# Revit family: Interrata - Copy - Copy (2)
name_source: partatom
category: Lighting Fixtures
revit_build: Autodesk Revit 2017 (Build: 20190507_1515(x64)
units: mm (PartAtom-declared; Revit-internal decimal feet)

## family parameters
Cut with Voids When Loaded = No
Host = Face
Light Source = No
OmniClass Number = 23.80.70.00
OmniClass Title = Lighting
Part Type = Normal
Room Calculation Point = No
Round Connector Dimension = Use Diameter
Shared = No

## types (10) — shared parameters
Apparent Load = 0 VA
Assembly Code = D5020200
BodyThickness_SYL = 3 mm  [stored 0.00984252 ft]
Chamfer_SYL = 2 mm  [stored 0.00656168 ft]
ClassificationName = Uniclass2015
ClassificationValue = EF_70_80
Default Elevation = 100 mm
IfcExportAs = IfcLightFixtureType
IfcExportType = IfcLightFixtureType
Keynote = 16500
Manufacturer = Feilo Sylvania
ManufacturerName = Feilo Sylvania
Material_1_SYL = Stainless Steel
Material_2_SYL = Polycarbonate, Clear
Material_3_SYL = <By Category>
Material_4_SYL = <By Category>
Thickness_SYL = 3 mm  [stored 0.00984252 ft]
Type Image = <None>
URL = http://www.sylvania-lighting.com
Voltage = 0 V
zero-valued in all types: Cost, NominalDepth, NominalHeight, NominalLength, PowerFactor

## per-type parameters (varying)
| type | BodyHeight1_SYL | BodyHeight2_SYL | BodyHeight3_SYL | BodyHeight4_SYL | BodyRad1_SYL | BodyRad2_SYL | BodyRad_SYL | DiffuserRad_SYL | L_SYL | Radius2_SYL | Radius3_SYL | Radius_SYL | RevolutionAxisFromRefLevel_SYL | RingHeight_SYL | S_SYL | Step1_SYL | Step2_SYL | TypeLamp_SYL | XS_SYL |
| 0049036 | 5 mm  [stored 0.0164042 ft] | 5 mm  [stored 0.0164042 ft] | 80 mm  [stored 0.262467 ft] | 6 mm  [stored 0.019685 ft] | 24 mm  [stored 0.0787402 ft] | 17 mm | 30 mm  [stored 0.0984252 ft] | 21 mm  [stored 0.0688976 ft] | No | 34 mm | 32 mm  [stored 0.104987 ft] | 50 mm  [stored 0.164042 ft] | 27 mm  [stored 0.0885827 ft] | 3 mm  [stored 0.00984252 ft] | No | 26 mm | 100 mm | Interrata Lamp : 0049036 INTERRATA XS  FROSTED 100LM 830 | Yes |
| 0049042 | 10 mm  [stored 0.0328084 ft] | 20 mm  [stored 0.0656168 ft] | 29 mm  [stored 0.0951444 ft] | 67 mm | 69 mm | 55 mm  [stored 0.180446 ft] | 95 mm | 66 mm  [stored 0.216535 ft] | No | 98 mm  [stored 0.321522 ft] | 96 mm  [stored 0.314961 ft] | 100 mm | 60 mm  [stored 0.19685 ft] | 3 mm  [stored 0.00984252 ft] | No | 18 mm | 206 mm | Interrata Lamp : 0049042 INTERRATA ADJUSTABLE M  CL 1000LM 830 MB | No |
| 0049043 | 10 mm  [stored 0.0328084 ft] | 20 mm  [stored 0.0656168 ft] | 29 mm  [stored 0.0951444 ft] | 67 mm | 69 mm | 55 mm  [stored 0.180446 ft] | 95 mm | 66 mm  [stored 0.216535 ft] | No | 98 mm  [stored 0.321522 ft] | 96 mm  [stored 0.314961 ft] | 100 mm | 60 mm  [stored 0.19685 ft] | 3 mm  [stored 0.00984252 ft] | No | 18 mm | 206 mm | Interrata Lamp : 0049043 INTERRATA ADJUSTABLE M  CL 1000LM 840 MB | No |
| 0049044 | 14 mm  [stored 0.0459318 ft] | 34 mm | 21 mm  [stored 0.0688976 ft] | 82 mm  [stored 0.269029 ft] | 99 mm | 83 mm | 120 mm | 94 mm  [stored 0.308399 ft] | Yes | 124 mm | 112 mm | 130 mm | 74 mm  [stored 0.242782 ft] | 4 mm  [stored 0.0131234 ft] | No | 20 mm  [stored 0.0656168 ft] | 236 mm | Interrata Lamp : 0049044 INTERRATA ADJUSTABLE L  CL 2000LM 830 MB | No |
| 0049037 | 5 mm  [stored 0.0164042 ft] | 5 mm  [stored 0.0164042 ft] | 80 mm  [stored 0.262467 ft] | 6 mm  [stored 0.019685 ft] | 24 mm  [stored 0.0787402 ft] | 17 mm | 30 mm  [stored 0.0984252 ft] | 21 mm  [stored 0.0688976 ft] | No | 34 mm | 32 mm  [stored 0.104987 ft] | 50 mm  [stored 0.164042 ft] | 27 mm  [stored 0.0885827 ft] | 3 mm  [stored 0.00984252 ft] | No | 26 mm | 100 mm | Interrata Lamp : 0049037 INTERRATA XS  FROSTED 100LM 840 | Yes |
| 0049039 | 5 mm  [stored 0.0164042 ft] | 5 mm  [stored 0.0164042 ft] | 80 mm  [stored 0.262467 ft] | 6 mm  [stored 0.019685 ft] | 24 mm  [stored 0.0787402 ft] | 17 mm | 30 mm  [stored 0.0984252 ft] | 21 mm  [stored 0.0688976 ft] | No | 34 mm | 32 mm  [stored 0.104987 ft] | 50 mm  [stored 0.164042 ft] | 27 mm  [stored 0.0885827 ft] | 3 mm  [stored 0.00984252 ft] | No | 26 mm | 100 mm | Interrata Lamp : 0049039 INTERRATA XS  CLEAR 100LM 840 NB | Yes |
| 0049038 | 5 mm  [stored 0.0164042 ft] | 5 mm  [stored 0.0164042 ft] | 80 mm  [stored 0.262467 ft] | 6 mm  [stored 0.019685 ft] | 24 mm  [stored 0.0787402 ft] | 17 mm | 30 mm  [stored 0.0984252 ft] | 21 mm  [stored 0.0688976 ft] | No | 34 mm | 32 mm  [stored 0.104987 ft] | 50 mm  [stored 0.164042 ft] | 27 mm  [stored 0.0885827 ft] | 3 mm  [stored 0.00984252 ft] | No | 26 mm | 100 mm | Interrata Lamp : 0049038 INTERRATA XS  CLEAR 100LM 830 NB | Yes |
| 0049040 | 4 mm  [stored 0.0131234 ft] | 6 mm  [stored 0.019685 ft] | 45 mm  [stored 0.147638 ft] | 45 mm  [stored 0.147638 ft] | 36 mm  [stored 0.11811 ft] | 36 mm  [stored 0.11811 ft] | 50 mm  [stored 0.164042 ft] | 33 mm  [stored 0.108268 ft] | No | 53 mm  [stored 0.173885 ft] | 42 mm | 60 mm  [stored 0.19685 ft] | 45 mm  [stored 0.147638 ft] | 3 mm  [stored 0.00984252 ft] | Yes | 15 mm  [stored 0.0492126 ft] | 121 mm | Interrata Lamp : 0049040 INTERRATA ADJUSTABLE S  CL 400LM 830 MB | No |
| 0049041 | 4 mm  [stored 0.0131234 ft] | 6 mm  [stored 0.019685 ft] | 45 mm  [stored 0.147638 ft] | 45 mm  [stored 0.147638 ft] | 36 mm  [stored 0.11811 ft] | 36 mm  [stored 0.11811 ft] | 50 mm  [stored 0.164042 ft] | 33 mm  [stored 0.108268 ft] | No | 53 mm  [stored 0.173885 ft] | 42 mm | 60 mm  [stored 0.19685 ft] | 45 mm  [stored 0.147638 ft] | 3 mm  [stored 0.00984252 ft] | Yes | 15 mm  [stored 0.0492126 ft] | 121 mm | Interrata Lamp : 0049041 INTERRATA ADJUSTABLE S  CL 400LM 840 MB | No |
| 0049045 | 14 mm  [stored 0.0459318 ft] | 34 mm | 21 mm  [stored 0.0688976 ft] | 82 mm  [stored 0.269029 ft] | 99 mm | 83 mm | 120 mm | 94 mm  [stored 0.308399 ft] | Yes | 124 mm | 112 mm | 130 mm | 74 mm  [stored 0.242782 ft] | 4 mm  [stored 0.0131234 ft] | No | 20 mm  [stored 0.0656168 ft] | 236 mm | Interrata Lamp : 0049045 INTERRATA ADJUSTABLE L  CL 2000LM 840 MB | No |

note: [stored X ft] marks values corroborated as IEEE doubles in the binary element streams (Revit-internal decimal feet)

## geometry (parser evidence)
native form markers: Sweep x5
no freeform markers — native parametric forms only
